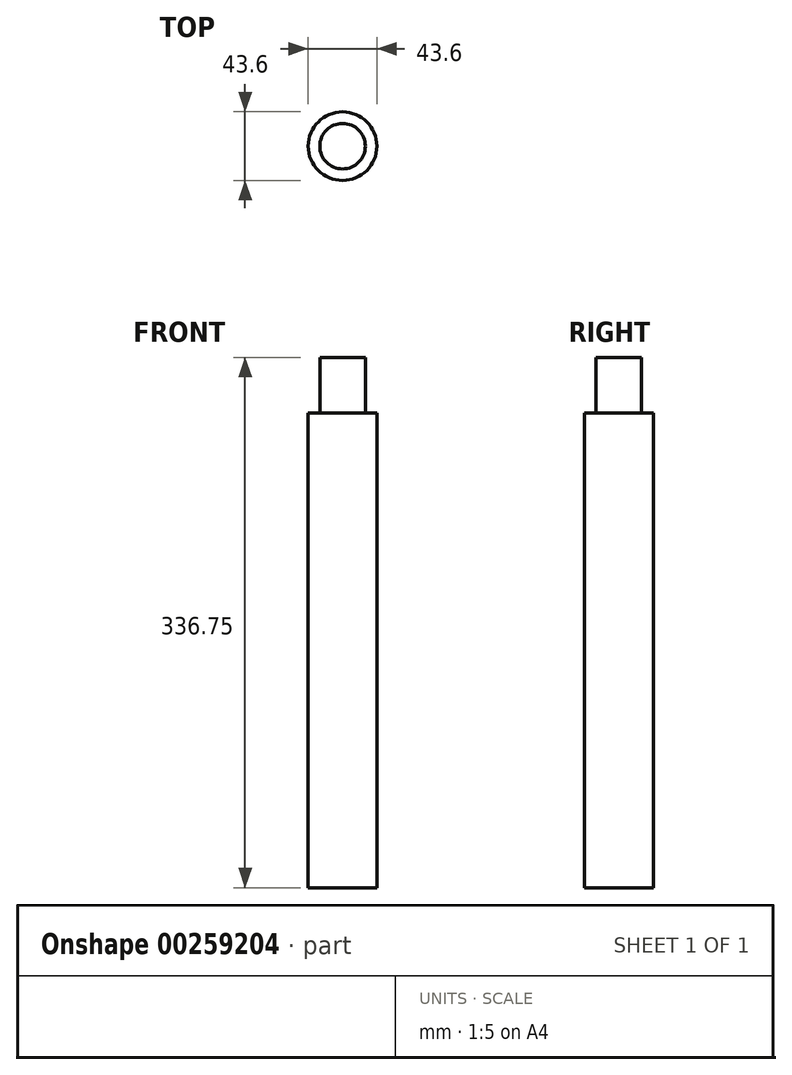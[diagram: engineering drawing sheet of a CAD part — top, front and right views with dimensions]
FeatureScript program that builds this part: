
annotation { "Feature Type Name" : "Feature", "Feature Type Description" : "" }
export const myFeature = defineFeature(function(context is Context, id is Id, definition is map)
    precondition{}
    {
        {
            var Q0;
            Q0=qCreatedBy(makeId("Top.planeOp"),FACE);
            var sketch = newSketch(context, id + "F0", { "sketchPlane" : qUnion([Q0])});
            skCircle(sketch, "E0", {"center": v(0, 0) * mm, "radius": 21.8 * mm});
            skSolve(sketch);
        }
        {
            var Q0;
            Q0=makeQuery(id+"F0.imprint","IMPRINT",FACE,{"disambiguationData":[TD([[makeQuery(id+"F0.imprint","IMPRINT",EDGE,{"derivedFrom":sQuery(id+"F0.wireOp",EDGE,"E0")}),1.0]])]});
            extrude(context, id + "F1", {"entities" : qUnion([Q0]), "depth" : 301.65 * mm});
        }
        {
            var Q0;
            Q0=makeQuery(id+"F1.opExtrude","CAP_FACE",FACE,{"disambiguationData":[OSD([sQuery(id+"F0.wireOp",EDGE,"E0")])],"isStart":false});
            var sketch = newSketch(context, id + "F2", { "sketchPlane" : qUnion([Q0])});
            skCircle(sketch, "E1", {"center": v(0, 0) * mm, "radius": 14.45 * mm});
            skSolve(sketch);
        }
        {
            var Q0;
            Q0=makeQuery(id+"F2.imprint","IMPRINT",FACE,{"disambiguationData":[TD([[makeQuery(id+"F2.imprint","IMPRINT",EDGE,{"derivedFrom":sQuery(id+"F2.wireOp",EDGE,"E1")}),1.0]])]});
            var Q1;
            Q1=sQuery(id+"F2.wireOp",EDGE,"E1");
            extrude(context, id + "F3", {"entities" : qUnion([Q0]), "surfaceEntities" : qUnion([Q1]), "depth" : 35.1 * mm});
        }
    });
